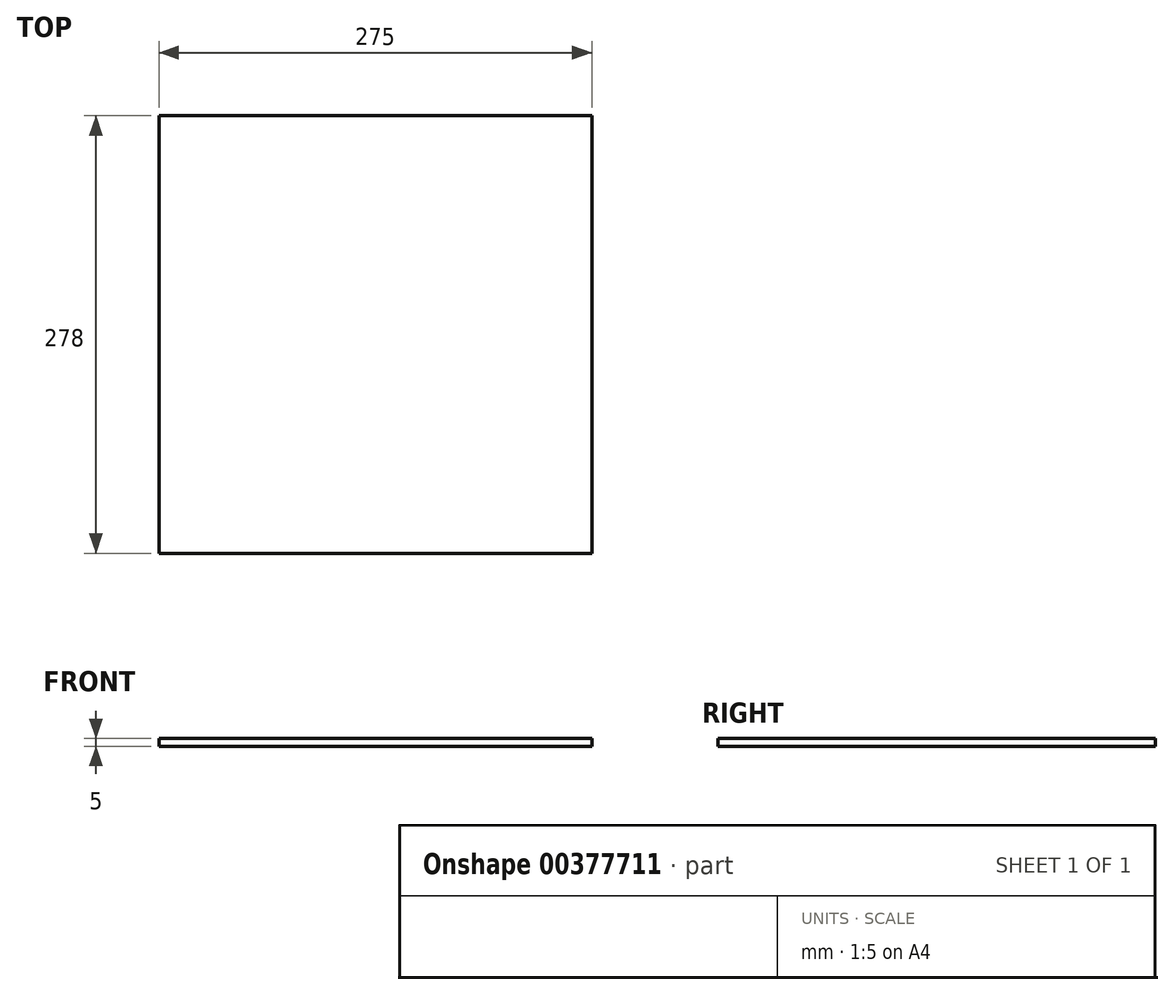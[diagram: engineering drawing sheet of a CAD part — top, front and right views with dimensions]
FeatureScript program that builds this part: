
annotation { "Feature Type Name" : "Feature", "Feature Type Description" : "" }
export const myFeature = defineFeature(function(context is Context, id is Id, definition is map)
    precondition{}
    {
        {
            var Q0;
            Q0=qCreatedBy(makeId("Top.planeOp"),FACE);
            var sketch = newSketch(context, id + "F0", { "sketchPlane" : qUnion([Q0])});
            skLineSegment(sketch, "E0.bottom", {"start": v(137.5, -139) * mm, "end": v(-137.5, -139) * mm});
            skLineSegment(sketch, "E0.top", {"start": v(137.5, 139) * mm, "end": v(-137.5, 139) * mm});
            skLineSegment(sketch, "E0.left", {"start": v(137.5, -139) * mm, "end": v(137.5, 139) * mm});
            skLineSegment(sketch, "E0.right", {"start": v(-137.5, -139) * mm, "end": v(-137.5, 139) * mm});
            skPoint(sketch, "E0.middle", {"position": v(0, 0) * mm});
            skSolve(sketch);
        }
        {
            var Q0;
            Q0 = qSketchRegion(id + "F0", true);
            extrude(context, id + "F1", {"entities" : qUnion([Q0]), "depth" : 5 * mm});
        }
    });
